# Revit family: Winmaster_Vandret Sidesamling (Winmaster Greenboard)
name_source: partatom
category: Detail Items
units: mm (PartAtom-declared; Revit-internal decimal feet)

## family parameters
Rotate with component = No
Section Shape = Not Defined
Shared = No

## types (1)
- Winmaster_Vandret Sidesamling (Winmaster Greenboard)
    Anvendelse = Monteres direkte på pladefalsen
    Brandklasse af pladefalsen = Brandklasse A1
    Description = Sidesamling m. indmuringsbeslag
    Funktion = Stabilisere pladefalsen ud mod formuren ved vinduer og dørhuller
    Indmuringsbeslag (mål) = Justerbar 66 mm
    Linjetab = 0,33 W/mK
    Manufacturer = WINMASTER
    Material_Harpun Klods = Plast
    Material_Indmuringsbeslag = Wall Base i PP og Wall Tie i Rustfrit Stål
    Material_Isolering = PU Skum
    Material_Mørtel = Limmørtel
    Material_Pladefalsen = Lysningsplade
    Samling af pladefalsen = Tappes ind i hinanden for at sikre
stabillitet og placering.Hjørner skal beklædes med net
    URL = https://winmaster.dk
    Udført af = Tegnestuen Tankestregen
    WINMASTER_Indmuringsbeslag = https://winmaster.dk
    WINMASTER_Pladefalse = https://winmaster.dk
    WINMASTER_URL = https://winmaster.dk

## geometry (parser evidence)
native form markers: Sweep x4
no freeform markers — native parametric forms only
